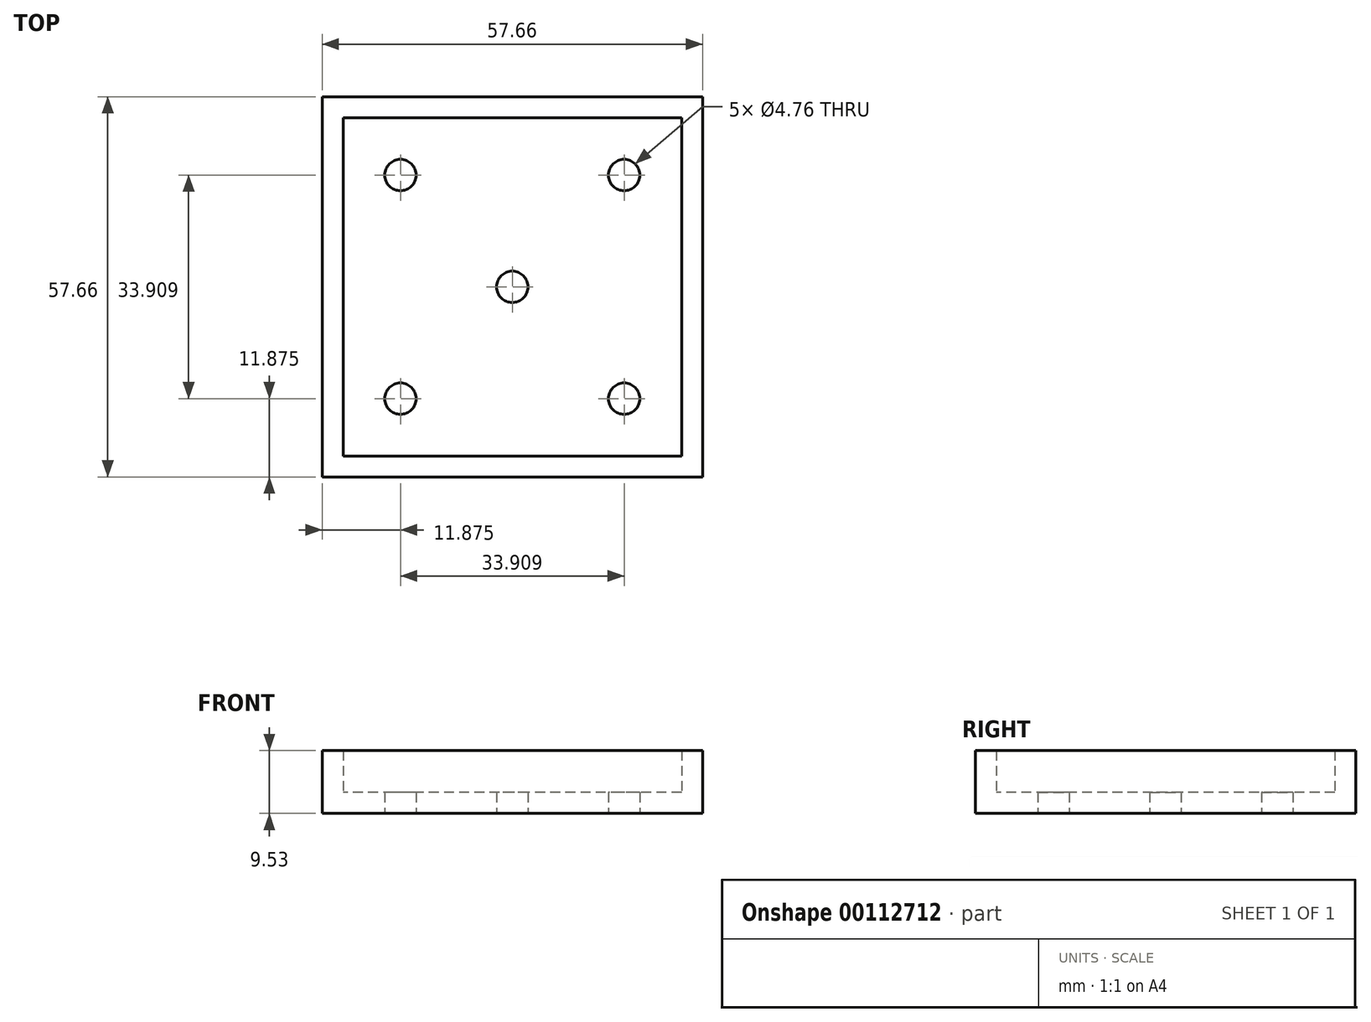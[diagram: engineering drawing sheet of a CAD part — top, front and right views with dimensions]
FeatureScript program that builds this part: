
annotation { "Feature Type Name" : "Feature", "Feature Type Description" : "" }
export const myFeature = defineFeature(function(context is Context, id is Id, definition is map)
    precondition{}
    {
        {
            var Q0;
            Q0=qCreatedBy(makeId("Top.planeOp"),FACE);
            var sketch = newSketch(context, id + "F0", { "sketchPlane" : qUnion([Q0])});
            skCircle(sketch, "E0", {"center": v(0, 0) * mm, "radius": 2.38 * mm});
            skLineSegment(sketch, "E1.bottom", {"start": v(28.83, -28.83) * mm, "end": v(-28.83, -28.83) * mm});
            skLineSegment(sketch, "E1.top", {"start": v(28.83, 28.83) * mm, "end": v(-28.83, 28.83) * mm});
            skLineSegment(sketch, "E1.left", {"start": v(28.83, -28.83) * mm, "end": v(28.83, 28.83) * mm});
            skLineSegment(sketch, "E1.right", {"start": v(-28.83, -28.83) * mm, "end": v(-28.83, 28.83) * mm});
            skLineSegment(sketch, "E2.bottom", {"start": v(16.95, 16.95) * mm, "end": v(-16.95, 16.95) * mm, "construction": true});
            skLineSegment(sketch, "E2.top", {"start": v(16.95, -16.95) * mm, "end": v(-16.95, -16.95) * mm, "construction": true});
            skLineSegment(sketch, "E2.left", {"start": v(16.95, 16.95) * mm, "end": v(16.95, -16.95) * mm, "construction": true});
            skLineSegment(sketch, "E2.right", {"start": v(-16.95, 16.95) * mm, "end": v(-16.95, -16.95) * mm, "construction": true});
            skCircle(sketch, "E3", {"center": v(-16.95, 16.95) * mm, "radius": 2.38 * mm});
            skCircle(sketch, "E4", {"center": v(16.95, 16.95) * mm, "radius": 2.38 * mm});
            skCircle(sketch, "E5", {"center": v(-16.95, -16.95) * mm, "radius": 2.38 * mm});
            skCircle(sketch, "E6", {"center": v(16.95, -16.95) * mm, "radius": 2.38 * mm});
            skSolve(sketch);
        }
        {
            var Q0;
            Q0=qSketchRegion(id+"F0",true);
            extrude(context, id + "F1", {"entities" : qUnion([Q0]), "depth" : 3.17 * mm});
        }
        {
            var Q0;
            Q0=makeQuery(id+"F1.opExtrude","CAP_FACE",FACE,{"disambiguationData":[OSD([sQuery(id+"F0.wireOp",EDGE,"E0"),sQuery(id+"F0.wireOp",EDGE,"E1.bottom"),sQuery(id+"F0.wireOp",EDGE,"E1.top"),sQuery(id+"F0.wireOp",EDGE,"E1.left"),sQuery(id+"F0.wireOp",EDGE,"E1.right"),sQuery(id+"F0.wireOp",EDGE,"E3"),sQuery(id+"F0.wireOp",EDGE,"E4"),sQuery(id+"F0.wireOp",EDGE,"E5"),sQuery(id+"F0.wireOp",EDGE,"E6")])],"isStart":false});
            var sketch = newSketch(context, id + "F2", { "sketchPlane" : qUnion([Q0])});
            skLineSegment(sketch, "E7.bottom", {"start": v(28.83, 28.83) * mm, "end": v(-28.83, 28.83) * mm});
            skLineSegment(sketch, "E7.top", {"start": v(28.83, -28.83) * mm, "end": v(-28.83, -28.83) * mm});
            skLineSegment(sketch, "E7.left", {"start": v(28.83, 28.83) * mm, "end": v(28.83, -28.83) * mm});
            skLineSegment(sketch, "E7.right", {"start": v(-28.83, 28.83) * mm, "end": v(-28.83, -28.83) * mm});
            skPoint(sketch, "E7.middle", {"position": v(0, 0) * mm});
            skLineSegment(sketch, "E8.bottom", {"start": v(25.65, 25.65) * mm, "end": v(-25.65, 25.65) * mm});
            skLineSegment(sketch, "E8.top", {"start": v(25.65, -25.65) * mm, "end": v(-25.65, -25.65) * mm});
            skLineSegment(sketch, "E8.left", {"start": v(25.65, 25.65) * mm, "end": v(25.65, -25.65) * mm});
            skLineSegment(sketch, "E8.right", {"start": v(-25.65, 25.65) * mm, "end": v(-25.65, -25.65) * mm});
            skSolve(sketch);
        }
        {
            var Q0;
            Q0 = qSketchRegion(id + "F2", true);
            extrude(context, id + "F3", {"entities" : qUnion([Q0]), "operationType" : NewBodyOperationType.ADD, "depth" : 6.35 * mm});
        }
    });
